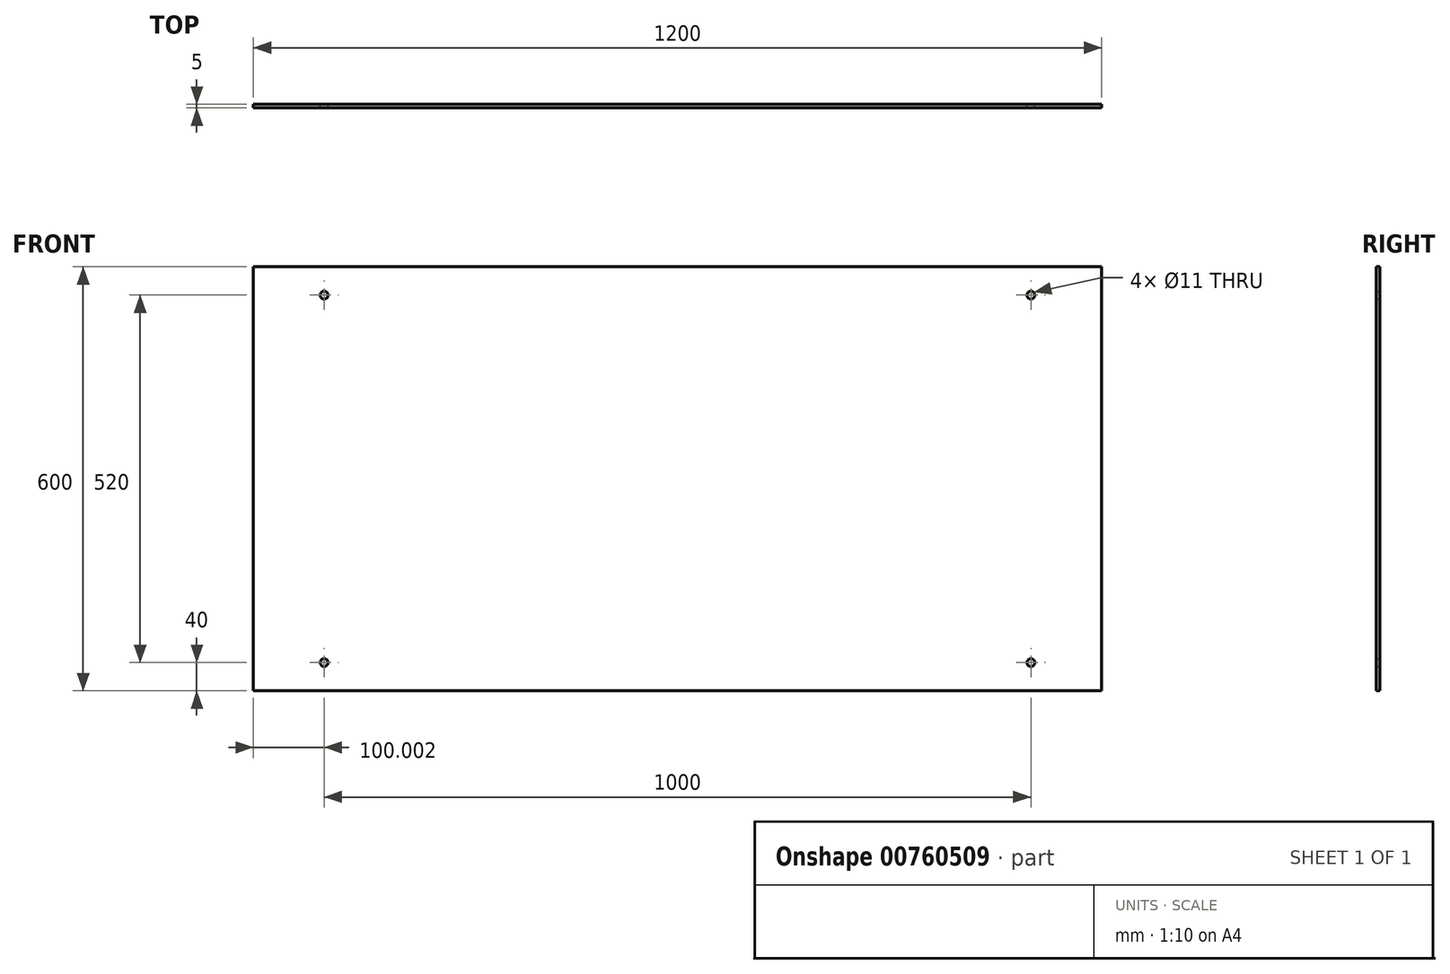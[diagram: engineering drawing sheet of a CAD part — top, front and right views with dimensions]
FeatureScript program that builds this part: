
annotation { "Feature Type Name" : "Feature", "Feature Type Description" : "" }
export const myFeature = defineFeature(function(context is Context, id is Id, definition is map)
    precondition{}
    {
        {
            var Q0;
            Q0=qCreatedBy(makeId("Front.planeOp"),FACE);
            var sketch = newSketch(context, id + "F0", { "sketchPlane" : qUnion([Q0])});
            skLineSegment(sketch, "E0.bottom", {"start": v(-66.97, 565.57) * mm, "end": v(1133.03, 565.57) * mm});
            skLineSegment(sketch, "E0.top", {"start": v(-66.97, -34.43) * mm, "end": v(1133.03, -34.43) * mm});
            skLineSegment(sketch, "E0.left", {"start": v(-66.97, 565.57) * mm, "end": v(-66.97, -34.43) * mm});
            skLineSegment(sketch, "E0.right", {"start": v(1133.03, 565.57) * mm, "end": v(1133.03, -34.43) * mm});
            skLineSegment(sketch, "E1", {"start": v(-66.97, 525.57) * mm, "end": v(1133.03, 525.57) * mm, "construction": true});
            skLineSegment(sketch, "E2", {"start": v(533.03, 565.57) * mm, "end": v(533.03, -34.43) * mm, "construction": true});
            skLineSegment(sketch, "E3", {"start": v(1033.03, 565.57) * mm, "end": v(1033.03, -34.43) * mm, "construction": true});
            skLineSegment(sketch, "E4", {"start": v(-66.97, 265.57) * mm, "end": v(1133.03, 265.57) * mm, "construction": true});
            skCircle(sketch, "E5", {"center": v(1033.03, 525.57) * mm, "radius": 5.5 * mm});
            skCircle(sketch, "E6.MirrorC", {"center": v(1033.03, 5.57) * mm, "radius": 5.5 * mm});
            skCircle(sketch, "E7.MirrorC", {"center": v(33.03, 5.57) * mm, "radius": 5.5 * mm});
            skCircle(sketch, "E8.MirrorC", {"center": v(33.03, 525.57) * mm, "radius": 5.5 * mm});
            skSolve(sketch);
        }
        {
            var Q0;
            Q0 = qSketchRegion(id + "F0", true);
            extrude(context, id + "F1", {"entities" : qUnion([Q0]), "depth" : 5 * mm, "offsetDistance" : 25 * mm});
        }
        {
            var Q0;
            Q0=makeQuery(id+"F1.opExtrude","CAP_FACE",FACE,{"disambiguationData":[OSD([sQuery(id+"F0.wireOp",EDGE,"E0.bottom"),sQuery(id+"F0.wireOp",EDGE,"E0.top"),sQuery(id+"F0.wireOp",EDGE,"E0.left"),sQuery(id+"F0.wireOp",EDGE,"E0.right"),sQuery(id+"F0.wireOp",EDGE,"E5"),sQuery(id+"F0.wireOp",EDGE,"E6.MirrorC"),sQuery(id+"F0.wireOp",EDGE,"E7.MirrorC"),sQuery(id+"F0.wireOp",EDGE,"E8.MirrorC")])],"isStart":false});
            var sketch = newSketch(context, id + "F2", { "sketchPlane" : qUnion([Q0])});
            skLineSegment(sketch, "E9", {"start": v(7.17, 540.57) * mm, "end": v(1058.9, 540.57) * mm});
            skLineSegment(sketch, "E10", {"start": v(1065.96, 543.5) * mm, "end": v(1199.1, 676.64) * mm});
            skLineSegment(sketch, "E11", {"start": v(1248.6, 627.14) * mm, "end": v(1095.96, 474.5) * mm});
            skLineSegment(sketch, "E12", {"start": v(1093.03, 467.43) * mm, "end": v(1093.03, 63.7) * mm});
            skLineSegment(sketch, "E13", {"start": v(1199.1, 676.64) * mm, "end": v(1248.6, 627.14) * mm});
            skLineSegment(sketch, "E14", {"start": v(533.03, 565.57) * mm, "end": v(533.03, -34.43) * mm, "construction": true});
            skLineSegment(sketch, "E15", {"start": v(-66.97, 265.57) * mm, "end": v(1133.03, 265.57) * mm, "construction": true});
            skLineSegment(sketch, "E16.MirrorCS", {"start": v(0.1, 543.5) * mm, "end": v(-133.03, 676.64) * mm});
            skLineSegment(sketch, "E17.MirrorCS", {"start": v(-182.53, 627.14) * mm, "end": v(-29.9, 474.5) * mm});
            skLineSegment(sketch, "E18.MirrorCS", {"start": v(-133.03, 676.64) * mm, "end": v(-182.53, 627.14) * mm});
            skLineSegment(sketch, "E19.MirrorCS", {"start": v(7.17, -9.43) * mm, "end": v(1058.9, -9.43) * mm});
            skLineSegment(sketch, "E20.MirrorCS", {"start": v(-182.53, -96) * mm, "end": v(-29.9, 56.64) * mm});
            skLineSegment(sketch, "E21.MirrorCS", {"start": v(0.1, -12.36) * mm, "end": v(-133.03, -145.5) * mm});
            skLineSegment(sketch, "E22.MirrorCS", {"start": v(-133.03, -145.5) * mm, "end": v(-182.53, -96) * mm});
            skLineSegment(sketch, "E23.MirrorCS", {"start": v(1199.1, -145.5) * mm, "end": v(1248.6, -96) * mm});
            skLineSegment(sketch, "E24.MirrorCS", {"start": v(1065.96, -12.36) * mm, "end": v(1199.1, -145.5) * mm});
            skLineSegment(sketch, "E25.MirrorCS", {"start": v(1248.6, -96) * mm, "end": v(1095.96, 56.64) * mm});
            skLineSegment(sketch, "E26", {"start": v(-26.97, 467.43) * mm, "end": v(-26.97, 63.7) * mm});
            skPoint(sketch, "E27.visualSharp", {"position": v(3.03, 540.57) * mm});
            skArc(sketch, "E27.filletArc", {"start": v(0.1, 543.5) * mm, "mid": v(3.35, 541.33) * mm, "end": v(7.17, 540.57) * mm});
            skPoint(sketch, "E28.visualSharp", {"position": v(-26.97, 471.58) * mm});
            skArc(sketch, "E28.filletArc", {"start": v(-26.97, 467.43) * mm, "mid": v(-27.73, 471.26) * mm, "end": v(-29.9, 474.5) * mm});
            skPoint(sketch, "E29.visualSharp", {"position": v(3.03, -9.43) * mm});
            skArc(sketch, "E29.filletArc", {"start": v(7.17, -9.43) * mm, "mid": v(3.35, -10.2) * mm, "end": v(0.1, -12.36) * mm});
            skPoint(sketch, "E30.visualSharp", {"position": v(-26.97, 59.56) * mm});
            skArc(sketch, "E30.filletArc", {"start": v(-29.9, 56.64) * mm, "mid": v(-27.73, 59.88) * mm, "end": v(-26.97, 63.7) * mm});
            skPoint(sketch, "E31.visualSharp", {"position": v(1063.03, 540.57) * mm});
            skArc(sketch, "E31.filletArc", {"start": v(1058.9, 540.57) * mm, "mid": v(1062.72, 541.33) * mm, "end": v(1065.96, 543.5) * mm});
            skPoint(sketch, "E32.visualSharp", {"position": v(1093.03, 471.58) * mm});
            skArc(sketch, "E32.filletArc", {"start": v(1095.96, 474.5) * mm, "mid": v(1093.8, 471.26) * mm, "end": v(1093.03, 467.43) * mm});
            skPoint(sketch, "E33.visualSharp", {"position": v(1063.03, -9.43) * mm});
            skArc(sketch, "E33.filletArc", {"start": v(1065.96, -12.36) * mm, "mid": v(1062.72, -10.2) * mm, "end": v(1058.9, -9.43) * mm});
            skPoint(sketch, "E34.newPointB", {"position": v(1093.03, 59.56) * mm});
            skArc(sketch, "E34.filletArc", {"start": v(1093.03, 63.7) * mm, "mid": v(1093.8, 59.88) * mm, "end": v(1095.96, 56.64) * mm});
            skArc(sketch, "E35.0", {"start": v(1098.03, 63.7) * mm, "mid": v(1098.41, 61.8) * mm, "end": v(1099.5, 60.17) * mm});
            skLineSegment(sketch, "E35.1", {"start": v(1255.67, -96) * mm, "end": v(1099.5, 60.17) * mm});
            skLineSegment(sketch, "E35.2", {"start": v(1199.1, -152.57) * mm, "end": v(1255.67, -96) * mm});
            skLineSegment(sketch, "E35.3", {"start": v(1062.43, -15.9) * mm, "end": v(1199.1, -152.57) * mm});
            skArc(sketch, "E35.4", {"start": v(1062.43, -15.9) * mm, "mid": v(1060.8, -14.81) * mm, "end": v(1058.9, -14.43) * mm});
            skLineSegment(sketch, "E35.5", {"start": v(7.17, -14.43) * mm, "end": v(1058.9, -14.43) * mm});
            skArc(sketch, "E35.6", {"start": v(-31.97, 467.43) * mm, "mid": v(-32.35, 469.35) * mm, "end": v(-33.43, 470.97) * mm});
            skLineSegment(sketch, "E35.7", {"start": v(-189.6, 627.14) * mm, "end": v(-33.43, 470.97) * mm});
            skLineSegment(sketch, "E35.8", {"start": v(-133.03, 683.7) * mm, "end": v(-189.6, 627.14) * mm});
            skLineSegment(sketch, "E35.9", {"start": v(3.64, 547.03) * mm, "end": v(-133.03, 683.7) * mm});
            skLineSegment(sketch, "E35.10", {"start": v(-31.97, 467.43) * mm, "end": v(-31.97, 63.7) * mm});
            skArc(sketch, "E35.11", {"start": v(-33.43, 60.17) * mm, "mid": v(-32.35, 61.8) * mm, "end": v(-31.97, 63.7) * mm});
            skLineSegment(sketch, "E35.12", {"start": v(-189.6, -96) * mm, "end": v(-33.43, 60.17) * mm});
            skLineSegment(sketch, "E35.13", {"start": v(-133.03, -152.57) * mm, "end": v(-189.6, -96) * mm});
            skLineSegment(sketch, "E35.14", {"start": v(3.64, -15.9) * mm, "end": v(-133.03, -152.57) * mm});
            skArc(sketch, "E35.15", {"start": v(7.17, -14.43) * mm, "mid": v(5.26, -14.81) * mm, "end": v(3.64, -15.9) * mm});
            skLineSegment(sketch, "E36.0", {"start": v(1098.03, 467.43) * mm, "end": v(1098.03, 63.7) * mm});
            skLineSegment(sketch, "E37.0", {"start": v(1255.67, 627.14) * mm, "end": v(1099.5, 470.97) * mm});
            skLineSegment(sketch, "E38.0", {"start": v(-71.97, 570.57) * mm, "end": v(-71.97, -39.43) * mm});
            skLineSegment(sketch, "E38.1", {"start": v(1138.03, 570.57) * mm, "end": v(-71.97, 570.57) * mm});
            skLineSegment(sketch, "E38.2", {"start": v(1138.03, -39.43) * mm, "end": v(1138.03, 570.57) * mm});
            skLineSegment(sketch, "E38.3", {"start": v(-71.97, -39.43) * mm, "end": v(1138.03, -39.43) * mm});
            skArc(sketch, "E39.0", {"start": v(1099.5, 470.97) * mm, "mid": v(1098.41, 469.35) * mm, "end": v(1098.03, 467.43) * mm});
            skLineSegment(sketch, "E40.0", {"start": v(1199.1, 683.7) * mm, "end": v(1255.67, 627.14) * mm});
            skLineSegment(sketch, "E41.0", {"start": v(1062.43, 547.03) * mm, "end": v(1199.1, 683.7) * mm});
            skArc(sketch, "E42.0", {"start": v(1058.9, 545.57) * mm, "mid": v(1060.8, 545.95) * mm, "end": v(1062.43, 547.03) * mm});
            skLineSegment(sketch, "E43.0", {"start": v(7.17, 545.57) * mm, "end": v(1058.9, 545.57) * mm});
            skArc(sketch, "E44.0", {"start": v(3.64, 547.03) * mm, "mid": v(5.26, 545.95) * mm, "end": v(7.17, 545.57) * mm});
            skSolve(sketch);
        }
        {
            var Q0;
            Q0=sQuery(id+"F2.wireOp",EDGE,"E10");
            var Q1;
            Q1=sQuery(id+"F2.wireOp",EDGE,"E37.0");
            var Q2;
            Q2=sQuery(id+"F2.wireOp",EDGE,"E40.0");
            var Q3;
            Q3=sQuery(id+"F2.wireOp",EDGE,"E35.9");
            var Q4;
            Q4=sQuery(id+"F2.wireOp",EDGE,"E35.7");
            var Q5;
            Q5=sQuery(id+"F2.wireOp",EDGE,"E35.8");
            var Q6;
            Q6=sQuery(id+"F2.wireOp",EDGE,"E26");
            var Q7;
            Q7=sQuery(id+"F2.wireOp",EDGE,"E35.10");
            var Q8;
            Q8=sQuery(id+"F2.wireOp",EDGE,"E35.11");
            var Q9;
            Q9=sQuery(id+"F2.wireOp",EDGE,"E30.filletArc");
            var Q10;
            Q10=sQuery(id+"F2.wireOp",EDGE,"E35.12");
            var Q11;
            Q11=sQuery(id+"F2.wireOp",EDGE,"E20.MirrorCS");
            var Q12;
            Q12=sQuery(id+"F2.wireOp",EDGE,"E35.13");
            var Q13;
            Q13=sQuery(id+"F2.wireOp",EDGE,"E22.MirrorCS");
            var Q14;
            Q14=sQuery(id+"F2.wireOp",EDGE,"E21.MirrorCS");
            var Q15;
            Q15=sQuery(id+"F2.wireOp",EDGE,"E35.14");
            var Q16;
            Q16=sQuery(id+"F2.wireOp",EDGE,"E29.filletArc");
            var Q17;
            Q17=sQuery(id+"F2.wireOp",EDGE,"E35.15");
            var Q18;
            Q18=sQuery(id+"F2.wireOp",EDGE,"E19.MirrorCS");
            var Q19;
            Q19=sQuery(id+"F2.wireOp",EDGE,"E35.5");
            var Q20;
            Q20=sQuery(id+"F2.wireOp",EDGE,"E28.filletArc");
            var Q21;
            Q21=sQuery(id+"F2.wireOp",EDGE,"E35.6");
            var Q22;
            Q22=sQuery(id+"F2.wireOp",EDGE,"E17.MirrorCS");
            var Q23;
            Q23=sQuery(id+"F2.wireOp",EDGE,"E18.MirrorCS");
            var Q24;
            Q24=sQuery(id+"F2.wireOp",EDGE,"E16.MirrorCS");
            var Q25;
            Q25=sQuery(id+"F2.wireOp",EDGE,"E9");
            var Q26;
            Q26=sQuery(id+"F2.wireOp",EDGE,"E43.0");
            var Q27;
            Q27=sQuery(id+"F2.wireOp",EDGE,"E27.filletArc");
            var Q28;
            Q28=sQuery(id+"F2.wireOp",EDGE,"E44.0");
            var Q29;
            Q29=sQuery(id+"F2.wireOp",EDGE,"E11");
            var Q30;
            Q30=sQuery(id+"F2.wireOp",EDGE,"E32.filletArc");
            var Q31;
            Q31=sQuery(id+"F2.wireOp",EDGE,"E39.0");
            var Q32;
            Q32=sQuery(id+"F2.wireOp",EDGE,"E36.0");
            var Q33;
            Q33=sQuery(id+"F2.wireOp",EDGE,"E12");
            var Q34;
            Q34=sQuery(id+"F2.wireOp",EDGE,"E41.0");
            var Q35;
            Q35=sQuery(id+"F2.wireOp",EDGE,"E31.filletArc");
            var Q36;
            Q36=sQuery(id+"F2.wireOp",EDGE,"E42.0");
            var Q37;
            Q37=sQuery(id+"F2.wireOp",EDGE,"E13");
            var Q38;
            Q38=sQuery(id+"F2.wireOp",EDGE,"E35.3");
            var Q39;
            Q39=sQuery(id+"F2.wireOp",EDGE,"E24.MirrorCS");
            var Q40;
            Q40=sQuery(id+"F2.wireOp",EDGE,"E33.filletArc");
            var Q41;
            Q41=sQuery(id+"F2.wireOp",EDGE,"E35.4");
            var Q42;
            Q42=sQuery(id+"F2.wireOp",EDGE,"E25.MirrorCS");
            var Q43;
            Q43=sQuery(id+"F2.wireOp",EDGE,"E35.1");
            var Q44;
            Q44=sQuery(id+"F2.wireOp",EDGE,"E23.MirrorCS");
            var Q45;
            Q45=sQuery(id+"F2.wireOp",EDGE,"E35.2");
            var Q46;
            Q46=sQuery(id+"F2.wireOp",EDGE,"E34.filletArc");
            var Q47;
            Q47=sQuery(id+"F2.wireOp",EDGE,"E35.0");
            extrude(context, id + "F3", {"bodyType" : ToolBodyType.SURFACE, "surfaceEntities" : qUnion([Q0, Q1, Q2, Q3, Q4, Q5, Q6, Q7, Q8, Q9, Q10, Q11, Q12, Q13, Q14, Q15, Q16, Q17, Q18, Q19, Q20, Q21, Q22, Q23, Q24, Q25, Q26, Q27, Q28, Q29, Q30, Q31, Q32, Q33, Q34, Q35, Q36, Q37, Q38, Q39, Q40, Q41, Q42, Q43, Q44, Q45, Q46, Q47]), "depth" : 80 * mm, "offsetDistance" : 25 * mm});
        }
    });
